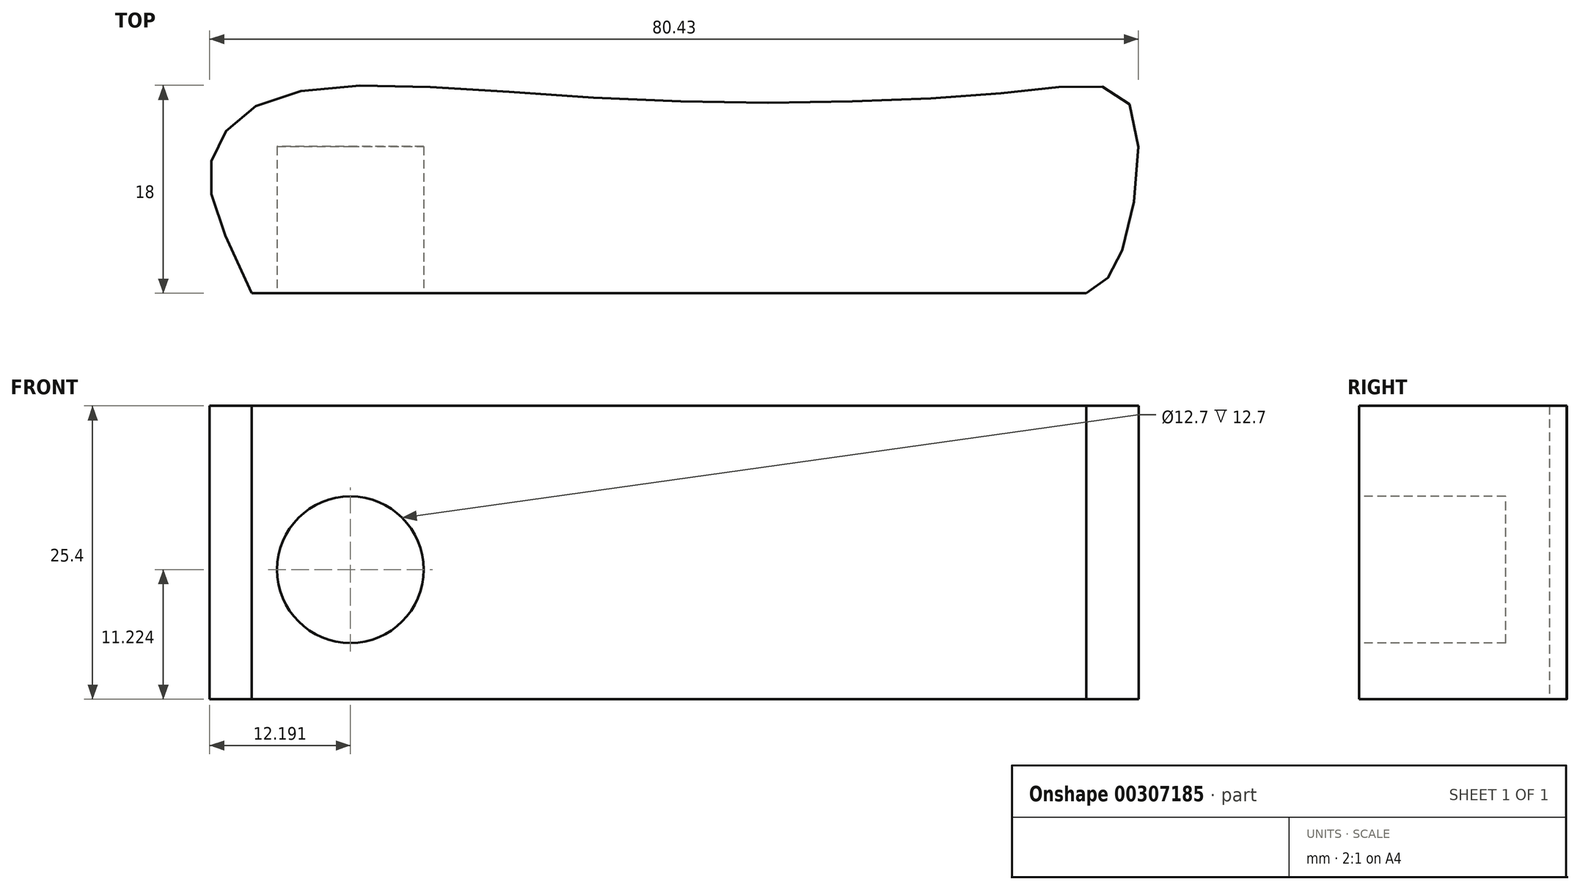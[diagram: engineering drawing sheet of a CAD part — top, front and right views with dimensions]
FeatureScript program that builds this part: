
annotation { "Feature Type Name" : "Feature", "Feature Type Description" : "" }
export const myFeature = defineFeature(function(context is Context, id is Id, definition is map)
    precondition{}
    {
        {
            var Q0;
            Q0=qCreatedBy(makeId("Top.planeOp"),FACE);
            var sketch = newSketch(context, id + "F0", { "sketchPlane" : qUnion([Q0])});
            skLineSegment(sketch, "E0", {"start": v(-47.97, 0) * mm, "end": v(24.3, 0) * mm});
            skFitSpline(sketch, "E1", {"points": [v(24.3, 0) * mm, v(27.14, 3) * mm, v(28.1, 16.25) * mm, v(18.94, 17.52) * mm, v(-17.67, 16.89) * mm, v(-46.08, 16.89) * mm, v(-51.45, 11.52) * mm, v(-47.97, 0) * mm], "startDerivative": vector(57.05, 33.8) * mm, "endDerivative": vector(64.9, -135.61) * mm});
            skSolve(sketch);
        }
        {
            var Q0;
            Q0=makeQuery(id+"F0.imprint","IMPRINT",FACE,{"disambiguationData":[TD([[makeQuery(id+"F0.imprint","IMPRINT",EDGE,{"derivedFrom":sQuery(id+"F0.wireOp",EDGE,"E0")}),1.0]])]});
            extrude(context, id + "F1", {"entities" : qUnion([Q0]), "depth" : 25.4 * mm});
        }
        {
            var Q0;
            Q0=qCreatedBy(makeId("Front.planeOp"),FACE);
            var sketch = newSketch(context, id + "F2", { "sketchPlane" : qUnion([Q0])});
            skCircle(sketch, "E2", {"center": v(-39.43, 11.22) * mm, "radius": 6.35 * mm});
            skSolve(sketch);
        }
        {
            var Q0;
            Q0 = qSketchRegion(id + "F2", true);
            extrude(context, id + "F3", {"entities" : qUnion([Q0]), "operationType" : NewBodyOperationType.REMOVE, "oppositeDirection" : true, "depth" : 12.7 * mm});
        }
    });
